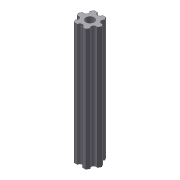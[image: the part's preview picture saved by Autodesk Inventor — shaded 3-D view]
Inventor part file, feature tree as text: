
AUTODESK INVENTOR PART (.ipt)
format: ipt  version: 2012 (Build 160160000, 160)  size: 95,744 bytes
history: native  units: in
note: dims shown in document units (in); Inventor stores cm internally (conversion verified against a paired STEP export)
features: extrude x2, sketch x2, pattern_circular x1
ambient origin geometry x8: Origin, YZ Plane, XZ Plane, XY Plane, X Axis, Y Axis, Z Axis, Center Point
bodies: Solid1 (feature_tree)
feature tree (5):
  extrude  "Extrusion1"  Depth=0.2in
  extrude  "Extrusion2"  Depth=0.0625in
  pattern_circular  "Circular Pattern1"  [2 undecoded]
  sketch  "Sketch1"  dims[d0=0.5in d1=0.2in]
  sketch  "Sketch2"  dims[d2=3.0in d3=0.0in d4=0.0625in d5=3.0in d6=0.0in d7=2.3622in d8=360.0deg]
note: 2 required parameter values undecoded (feature->parameter linkage not recoverable at this tier; creation-order binding heuristic only, values carry confidence <= 0.55)
